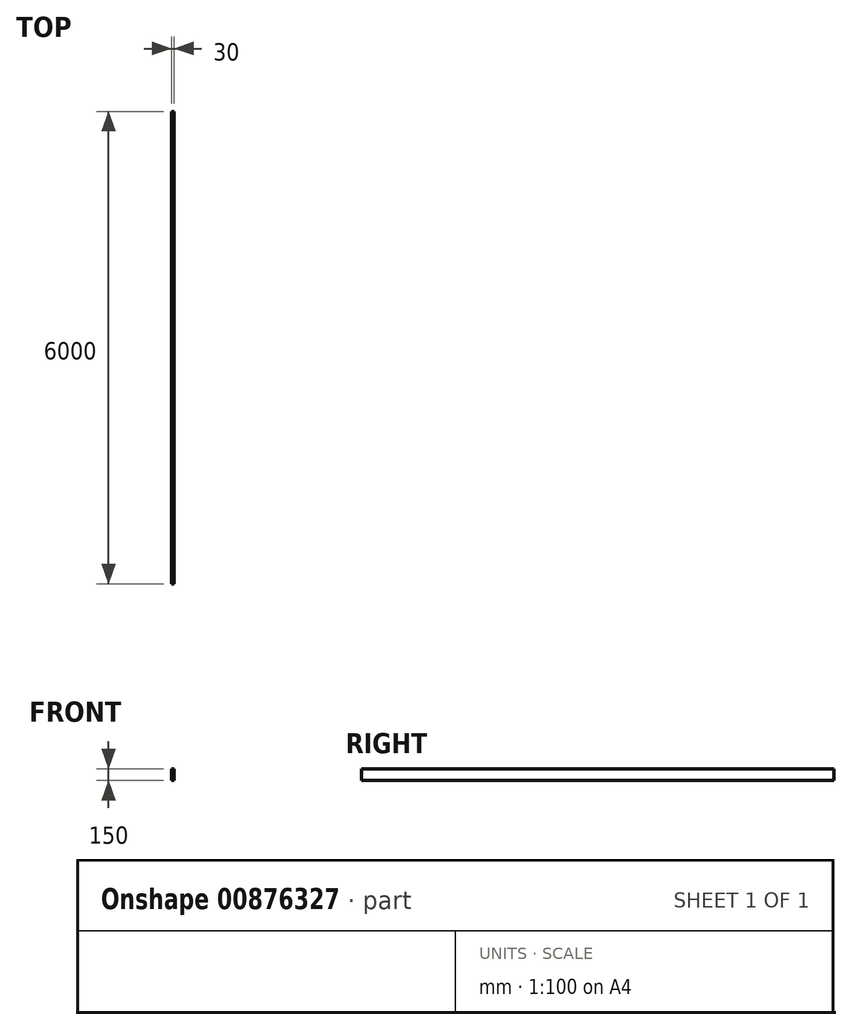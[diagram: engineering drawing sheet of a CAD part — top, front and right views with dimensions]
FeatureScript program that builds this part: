
annotation { "Feature Type Name" : "Feature", "Feature Type Description" : "" }
export const myFeature = defineFeature(function(context is Context, id is Id, definition is map)
    precondition{}
    {
        {
            var Q0;
            Q0=qCreatedBy(makeId("Front.planeOp"),FACE);
            var sketch = newSketch(context, id + "F0", { "sketchPlane" : qUnion([Q0])});
            skLineSegment(sketch, "E0", {"start": v(0, 0) * mm, "end": v(0, 150) * mm});
            skLineSegment(sketch, "E1", {"start": v(0, 150) * mm, "end": v(-30, 150) * mm});
            skLineSegment(sketch, "E2", {"start": v(-30, 150) * mm, "end": v(-30, 0) * mm});
            skLineSegment(sketch, "E3", {"start": v(-30, 0) * mm, "end": v(0, 0) * mm});
            skSolve(sketch);
        }
        {
            var Q0;
            Q0=qCreatedBy(makeId("Right.planeOp"),FACE);
            var sketch = newSketch(context, id + "F1", { "sketchPlane" : qUnion([Q0])});
            skLineSegment(sketch, "E4", {"start": v(0, 0) * mm, "end": v(-6000, 0) * mm});
            skSolve(sketch);
        }
        {
            var Q0;
            Q0=makeQuery(id+"F0.imprint","IMPRINT",FACE,{"disambiguationData":[TD([[makeQuery(id+"F0.imprint","IMPRINT",EDGE,{"derivedFrom":sQuery(id+"F0.wireOp",EDGE,"E0")}),1.0]])]});
            var Q1;
            Q1=sQuery(id+"F1.wireOp",EDGE,"E4");
            sweep(context, id + "F2", {"profiles" : qUnion([Q0]), "path" : qUnion([Q1])});
        }
    });
